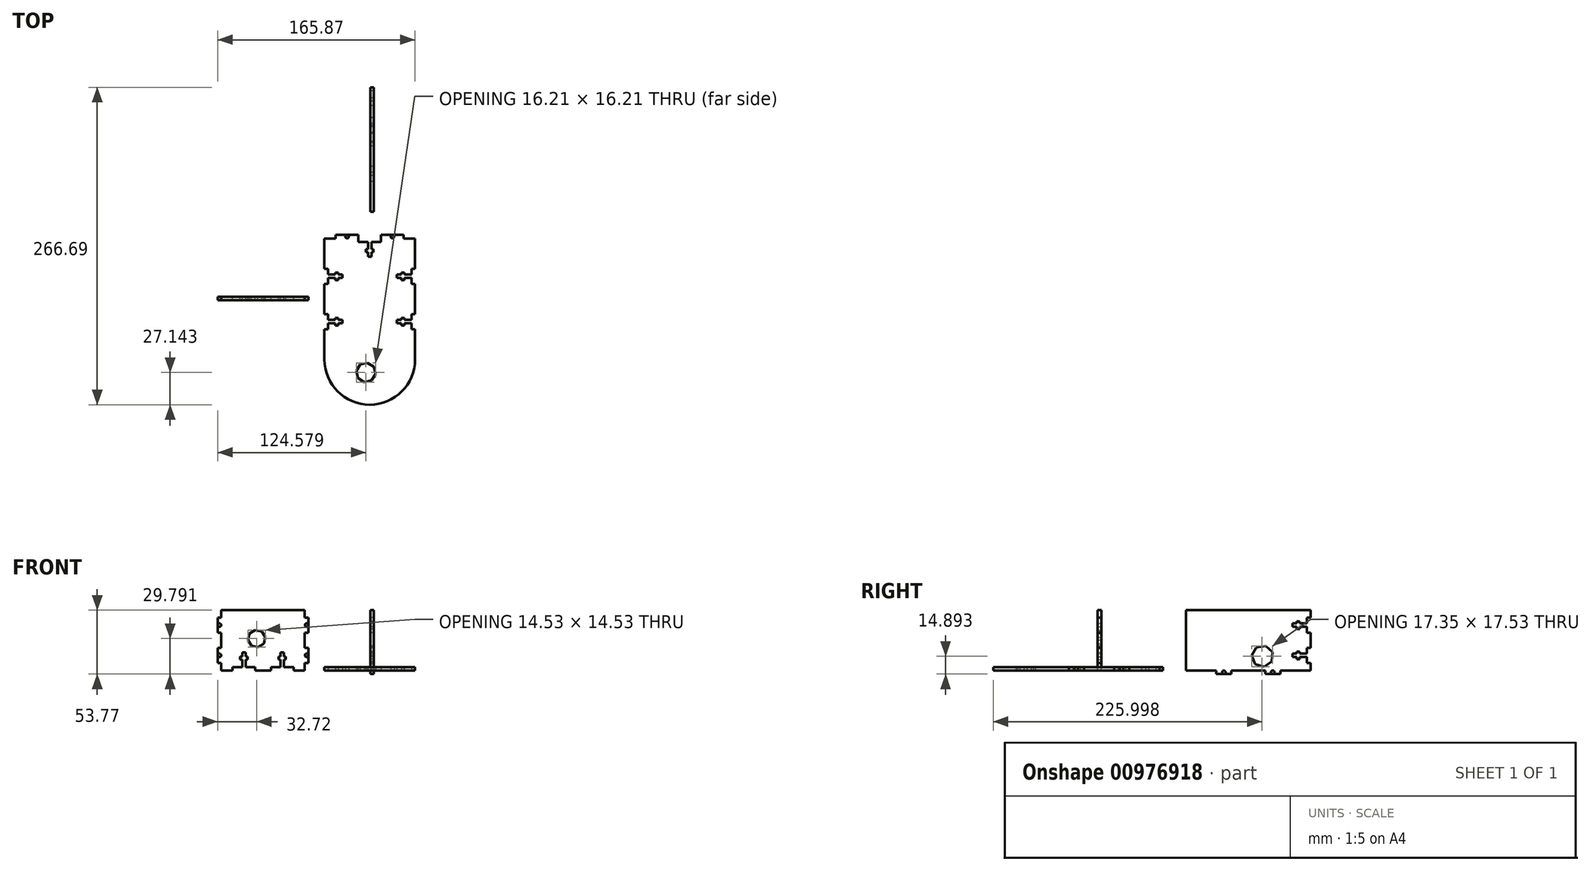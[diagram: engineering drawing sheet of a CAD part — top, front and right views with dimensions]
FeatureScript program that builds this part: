
annotation { "Feature Type Name" : "Feature", "Feature Type Description" : "" }
export const myFeature = defineFeature(function(context is Context, id is Id, definition is map)
    precondition{}
    {
        {
            var Q0;
            Q0=qCreatedBy(makeId("Top.planeOp"),FACE);
            var sketch = newSketch(context, id + "F0", { "sketchPlane" : qUnion([Q0])});
            skLineSegment(sketch, "E0.bottom", {"start": v(-38.64, 48.88) * mm, "end": v(-29.12, 48.88) * mm});
            skLineSegment(sketch, "E0.left", {"start": v(-38.64, 48.88) * mm, "end": v(-38.64, 23.48) * mm});
            skLineSegment(sketch, "E0.right", {"start": v(37.56, 48.88) * mm, "end": v(37.56, 23.48) * mm});
            skCircle(sketch, "E1", {"center": v(-19.6, 50.33) * mm, "radius": 1.42 * mm});
            skCircle(sketch, "E2", {"center": v(18.5, 50.33) * mm, "radius": 1.42 * mm});
            skLineSegment(sketch, "E3.bottom", {"start": v(-29.12, 51.85) * mm, "end": v(-10.07, 51.85) * mm});
            skLineSegment(sketch, "E3.left", {"start": v(-29.12, 51.85) * mm, "end": v(-29.12, 48.88) * mm});
            skLineSegment(sketch, "E3.right", {"start": v(-10.07, 51.85) * mm, "end": v(-10.07, 48.88) * mm});
            skLineSegment(sketch, "E4.top", {"start": v(28.03, 51.85) * mm, "end": v(8.98, 51.85) * mm});
            skLineSegment(sketch, "E4.left", {"start": v(28.03, 48.88) * mm, "end": v(28.03, 51.85) * mm});
            skLineSegment(sketch, "E4.right", {"start": v(8.98, 48.88) * mm, "end": v(8.98, 51.85) * mm});
            skLineSegment(sketch, "E5", {"start": v(-10.07, 48.88) * mm, "end": v(-10.07, 45.9) * mm});
            skLineSegment(sketch, "E6", {"start": v(-10.07, 45.9) * mm, "end": v(-1.96, 45.9) * mm});
            skLineSegment(sketch, "E7", {"start": v(8.98, 45.9) * mm, "end": v(8.98, 48.88) * mm});
            skLineSegment(sketch, "E8", {"start": v(-1.96, 45.9) * mm, "end": v(-1.96, 39.76) * mm});
            skLineSegment(sketch, "E9", {"start": v(-1.96, 39.76) * mm, "end": v(-3.7, 39.76) * mm});
            skLineSegment(sketch, "E10", {"start": v(-3.7, 39.76) * mm, "end": v(-3.7, 37.22) * mm});
            skLineSegment(sketch, "E11", {"start": v(-3.7, 37.22) * mm, "end": v(-1.96, 37.22) * mm});
            skLineSegment(sketch, "E12", {"start": v(-1.96, 37.22) * mm, "end": v(-1.96, 33.64) * mm});
            skLineSegment(sketch, "E13", {"start": v(-1.96, 33.64) * mm, "end": v(0.88, 33.64) * mm});
            skLineSegment(sketch, "E14", {"start": v(0.88, 33.64) * mm, "end": v(0.88, 37.22) * mm});
            skLineSegment(sketch, "E15", {"start": v(0.88, 37.22) * mm, "end": v(2.6, 37.22) * mm});
            skLineSegment(sketch, "E16", {"start": v(2.6, 37.22) * mm, "end": v(2.6, 39.76) * mm});
            skLineSegment(sketch, "E17", {"start": v(2.6, 39.76) * mm, "end": v(0.88, 39.76) * mm});
            skLineSegment(sketch, "E18", {"start": v(0.88, 39.76) * mm, "end": v(0.88, 45.9) * mm});
            skLineSegment(sketch, "E19.trimOffspring", {"start": v(28.03, 48.88) * mm, "end": v(37.56, 48.88) * mm});
            skLineSegment(sketch, "E20.bottom", {"start": v(37.56, 23.48) * mm, "end": v(34.59, 23.48) * mm});
            skLineSegment(sketch, "E20.top", {"start": v(37.56, 10.78) * mm, "end": v(34.59, 10.78) * mm});
            skLineSegment(sketch, "E20.right", {"start": v(34.59, 23.48) * mm, "end": v(34.59, 18.55) * mm});
            skLineSegment(sketch, "E21", {"start": v(34.59, 18.55) * mm, "end": v(28.44, 18.55) * mm});
            skLineSegment(sketch, "E22", {"start": v(28.44, 18.55) * mm, "end": v(28.44, 20.28) * mm});
            skLineSegment(sketch, "E23", {"start": v(28.44, 20.28) * mm, "end": v(25.9, 20.28) * mm});
            skLineSegment(sketch, "E24", {"start": v(25.9, 20.28) * mm, "end": v(25.9, 18.55) * mm});
            skLineSegment(sketch, "E25", {"start": v(25.9, 18.55) * mm, "end": v(22.32, 18.55) * mm});
            skLineSegment(sketch, "E26", {"start": v(22.32, 18.55) * mm, "end": v(22.32, 15.7) * mm});
            skLineSegment(sketch, "E27", {"start": v(22.32, 15.7) * mm, "end": v(25.9, 15.7) * mm});
            skLineSegment(sketch, "E28", {"start": v(25.9, 15.7) * mm, "end": v(25.9, 13.98) * mm});
            skLineSegment(sketch, "E29", {"start": v(25.9, 13.98) * mm, "end": v(28.44, 13.98) * mm});
            skLineSegment(sketch, "E30", {"start": v(28.44, 13.98) * mm, "end": v(28.44, 15.7) * mm});
            skLineSegment(sketch, "E31", {"start": v(28.44, 15.7) * mm, "end": v(34.59, 15.7) * mm});
            skLineSegment(sketch, "E32.trimOffspring", {"start": v(0.88, 45.9) * mm, "end": v(8.98, 45.9) * mm});
            skLineSegment(sketch, "E33", {"start": v(37.56, -14.62) * mm, "end": v(34.59, -14.62) * mm});
            skLineSegment(sketch, "E34", {"start": v(34.59, -14.62) * mm, "end": v(34.59, -19.55) * mm});
            skLineSegment(sketch, "E35", {"start": v(34.59, -27.32) * mm, "end": v(37.56, -27.32) * mm});
            skLineSegment(sketch, "E36.trimOffspring", {"start": v(34.59, 15.7) * mm, "end": v(34.59, 10.78) * mm});
            skLineSegment(sketch, "E37.trimOffspring", {"start": v(37.56, 10.78) * mm, "end": v(37.56, -14.62) * mm});
            skLineSegment(sketch, "E38", {"start": v(34.59, -19.55) * mm, "end": v(28.44, -19.55) * mm});
            skLineSegment(sketch, "E39", {"start": v(28.44, -19.55) * mm, "end": v(28.44, -17.82) * mm});
            skLineSegment(sketch, "E40", {"start": v(28.44, -17.82) * mm, "end": v(25.9, -17.82) * mm});
            skLineSegment(sketch, "E41", {"start": v(25.9, -17.82) * mm, "end": v(25.9, -19.55) * mm});
            skLineSegment(sketch, "E42", {"start": v(25.9, -19.55) * mm, "end": v(22.32, -19.55) * mm});
            skLineSegment(sketch, "E43", {"start": v(22.32, -19.55) * mm, "end": v(22.32, -22.4) * mm});
            skLineSegment(sketch, "E44", {"start": v(22.32, -22.4) * mm, "end": v(25.9, -22.4) * mm});
            skLineSegment(sketch, "E45", {"start": v(25.9, -22.4) * mm, "end": v(25.9, -24.12) * mm});
            skLineSegment(sketch, "E46", {"start": v(25.9, -24.12) * mm, "end": v(28.44, -24.12) * mm});
            skLineSegment(sketch, "E47", {"start": v(28.44, -24.12) * mm, "end": v(28.44, -22.4) * mm});
            skLineSegment(sketch, "E48", {"start": v(28.44, -22.4) * mm, "end": v(34.59, -22.4) * mm});
            skLineSegment(sketch, "E49.trimOffspring", {"start": v(37.56, -27.32) * mm, "end": v(37.56, -52.72) * mm});
            skLineSegment(sketch, "E50.trimOffspring", {"start": v(34.59, -22.4) * mm, "end": v(34.59, -27.32) * mm});
            skLineSegment(sketch, "E51", {"start": v(-38.64, -27.32) * mm, "end": v(-35.67, -27.32) * mm});
            skLineSegment(sketch, "E52", {"start": v(-35.67, -27.32) * mm, "end": v(-35.67, -22.4) * mm});
            skLineSegment(sketch, "E53", {"start": v(-35.67, -14.62) * mm, "end": v(-38.64, -14.62) * mm});
            skLineSegment(sketch, "E54", {"start": v(-35.67, -22.4) * mm, "end": v(-29.52, -22.4) * mm});
            skLineSegment(sketch, "E55", {"start": v(-29.52, -22.4) * mm, "end": v(-29.52, -24.12) * mm});
            skLineSegment(sketch, "E56", {"start": v(-29.52, -24.12) * mm, "end": v(-26.98, -24.12) * mm});
            skLineSegment(sketch, "E57", {"start": v(-26.98, -24.12) * mm, "end": v(-26.98, -22.4) * mm});
            skLineSegment(sketch, "E58", {"start": v(-26.98, -22.4) * mm, "end": v(-23.4, -22.4) * mm});
            skLineSegment(sketch, "E59", {"start": v(-23.4, -22.4) * mm, "end": v(-23.4, -19.55) * mm});
            skLineSegment(sketch, "E60", {"start": v(-23.4, -19.55) * mm, "end": v(-26.98, -19.55) * mm});
            skLineSegment(sketch, "E61", {"start": v(-26.98, -19.55) * mm, "end": v(-26.98, -17.82) * mm});
            skLineSegment(sketch, "E62", {"start": v(-26.98, -17.82) * mm, "end": v(-29.52, -17.82) * mm});
            skLineSegment(sketch, "E63", {"start": v(-29.52, -17.82) * mm, "end": v(-29.52, -19.55) * mm});
            skLineSegment(sketch, "E64", {"start": v(-29.52, -19.55) * mm, "end": v(-35.67, -19.55) * mm});
            skLineSegment(sketch, "E65.trimOffspring", {"start": v(-35.67, -19.55) * mm, "end": v(-35.67, -14.62) * mm});
            skLineSegment(sketch, "E66.trimOffspring", {"start": v(-38.64, -27.32) * mm, "end": v(-38.64, -52.72) * mm});
            skLineSegment(sketch, "E67", {"start": v(-38.64, 23.48) * mm, "end": v(-35.67, 23.48) * mm});
            skLineSegment(sketch, "E68", {"start": v(-35.67, 23.48) * mm, "end": v(-35.67, 18.55) * mm});
            skLineSegment(sketch, "E69", {"start": v(-35.67, 10.78) * mm, "end": v(-38.64, 10.78) * mm});
            skLineSegment(sketch, "E70", {"start": v(-35.67, 18.55) * mm, "end": v(-29.52, 18.55) * mm});
            skLineSegment(sketch, "E71", {"start": v(-29.52, 18.55) * mm, "end": v(-29.52, 20.28) * mm});
            skLineSegment(sketch, "E72", {"start": v(-29.52, 20.28) * mm, "end": v(-26.98, 20.28) * mm});
            skLineSegment(sketch, "E73", {"start": v(-26.98, 20.28) * mm, "end": v(-26.98, 18.55) * mm});
            skLineSegment(sketch, "E74", {"start": v(-26.98, 18.55) * mm, "end": v(-23.4, 18.55) * mm});
            skLineSegment(sketch, "E75", {"start": v(-23.4, 18.55) * mm, "end": v(-23.4, 15.7) * mm});
            skLineSegment(sketch, "E76", {"start": v(-23.4, 15.7) * mm, "end": v(-26.98, 15.7) * mm});
            skLineSegment(sketch, "E77", {"start": v(-26.98, 15.7) * mm, "end": v(-26.98, 13.98) * mm});
            skLineSegment(sketch, "E78", {"start": v(-26.98, 13.98) * mm, "end": v(-29.52, 13.98) * mm});
            skLineSegment(sketch, "E79", {"start": v(-29.52, 13.98) * mm, "end": v(-29.52, 15.7) * mm});
            skLineSegment(sketch, "E80", {"start": v(-29.52, 15.7) * mm, "end": v(-35.67, 15.7) * mm});
            skLineSegment(sketch, "E81.trimOffspring", {"start": v(-35.67, 15.7) * mm, "end": v(-35.67, 10.78) * mm});
            skLineSegment(sketch, "E82.trimOffspring", {"start": v(-38.64, 10.78) * mm, "end": v(-38.64, -14.62) * mm});
            skArc(sketch, "E83", {"start": v(-38.64, -52.72) * mm, "mid": v(-0.54, -90.82) * mm, "end": v(37.56, -52.72) * mm});
            skLineSegment(sketch, "E84.0", {"start": v(4.37, -65.01) * mm, "end": v(1.06, -70.35) * mm});
            skLineSegment(sketch, "E84.1", {"start": v(1.06, -70.35) * mm, "end": v(-5.07, -71.78) * mm});
            skLineSegment(sketch, "E84.2", {"start": v(-5.07, -71.78) * mm, "end": v(-10.4, -68.46) * mm});
            skLineSegment(sketch, "E84.3", {"start": v(-10.4, -68.46) * mm, "end": v(-11.84, -62.34) * mm});
            skLineSegment(sketch, "E84.4", {"start": v(-11.84, -62.34) * mm, "end": v(-8.52, -57) * mm});
            skLineSegment(sketch, "E84.5", {"start": v(-8.52, -57) * mm, "end": v(-2.4, -55.57) * mm});
            skLineSegment(sketch, "E84.6", {"start": v(-2.4, -55.57) * mm, "end": v(2.94, -58.9) * mm});
            skLineSegment(sketch, "E84.7", {"start": v(2.94, -58.9) * mm, "end": v(4.37, -65.01) * mm});
            skPoint(sketch, "E84.0.midPoint", {"position": v(2.71, -67.68) * mm});
            skSolve(sketch);
        }
        {
            var Q0;
            Q0=qCreatedBy(makeId("Right.planeOp"),FACE);
            var sketch = newSketch(context, id + "F1", { "sketchPlane" : qUnion([Q0])});
            skLineSegment(sketch, "E85", {"start": v(71.3, 0) * mm, "end": v(96.7, 0) * mm});
            skLineSegment(sketch, "E86", {"start": v(175.87, 0) * mm, "end": v(175.87, 6.35) * mm});
            skLineSegment(sketch, "E87", {"start": v(175.87, 50.8) * mm, "end": v(71.3, 50.8) * mm});
            skLineSegment(sketch, "E88", {"start": v(71.3, 50.8) * mm, "end": v(71.3, 44.45) * mm});
            skLineSegment(sketch, "E89", {"start": v(175.87, 44.45) * mm, "end": v(172.9, 44.45) * mm});
            skLineSegment(sketch, "E90", {"start": v(172.9, 44.45) * mm, "end": v(172.9, 39.52) * mm});
            skLineSegment(sketch, "E91", {"start": v(172.9, 31.75) * mm, "end": v(175.87, 31.75) * mm});
            skLineSegment(sketch, "E92", {"start": v(175.87, 19.05) * mm, "end": v(172.9, 19.05) * mm});
            skLineSegment(sketch, "E93", {"start": v(172.9, 19.05) * mm, "end": v(172.9, 14.12) * mm});
            skLineSegment(sketch, "E94", {"start": v(172.9, 6.35) * mm, "end": v(175.87, 6.35) * mm});
            skLineSegment(sketch, "E95", {"start": v(172.9, 39.52) * mm, "end": v(166.75, 39.52) * mm});
            skLineSegment(sketch, "E96", {"start": v(166.75, 39.52) * mm, "end": v(166.75, 41.25) * mm});
            skLineSegment(sketch, "E97", {"start": v(166.75, 41.25) * mm, "end": v(164.2, 41.25) * mm});
            skLineSegment(sketch, "E98", {"start": v(164.2, 41.25) * mm, "end": v(164.2, 39.52) * mm});
            skLineSegment(sketch, "E99", {"start": v(164.2, 39.52) * mm, "end": v(160.63, 39.52) * mm});
            skLineSegment(sketch, "E100", {"start": v(160.63, 39.52) * mm, "end": v(160.63, 36.68) * mm});
            skLineSegment(sketch, "E101", {"start": v(160.63, 36.68) * mm, "end": v(164.2, 36.68) * mm});
            skLineSegment(sketch, "E102", {"start": v(164.2, 36.68) * mm, "end": v(164.2, 34.95) * mm});
            skLineSegment(sketch, "E103", {"start": v(164.2, 34.95) * mm, "end": v(166.75, 34.95) * mm});
            skLineSegment(sketch, "E104", {"start": v(166.75, 34.95) * mm, "end": v(166.75, 36.68) * mm});
            skLineSegment(sketch, "E105", {"start": v(166.75, 36.68) * mm, "end": v(172.9, 36.68) * mm});
            skLineSegment(sketch, "E106.trimOffspring", {"start": v(172.9, 36.68) * mm, "end": v(172.9, 31.75) * mm});
            skLineSegment(sketch, "E107.trimOffspring", {"start": v(175.87, 44.45) * mm, "end": v(175.87, 50.8) * mm});
            skLineSegment(sketch, "E108", {"start": v(172.9, 14.12) * mm, "end": v(166.75, 14.12) * mm});
            skLineSegment(sketch, "E109", {"start": v(166.75, 14.12) * mm, "end": v(166.75, 15.85) * mm});
            skLineSegment(sketch, "E110", {"start": v(166.75, 15.85) * mm, "end": v(164.2, 15.85) * mm});
            skLineSegment(sketch, "E111", {"start": v(164.2, 15.85) * mm, "end": v(164.2, 14.12) * mm});
            skLineSegment(sketch, "E112", {"start": v(164.2, 14.12) * mm, "end": v(160.63, 14.12) * mm});
            skLineSegment(sketch, "E113", {"start": v(160.63, 14.12) * mm, "end": v(160.63, 11.28) * mm});
            skLineSegment(sketch, "E114", {"start": v(160.63, 11.28) * mm, "end": v(164.2, 11.28) * mm});
            skLineSegment(sketch, "E115", {"start": v(164.2, 11.28) * mm, "end": v(164.2, 9.55) * mm});
            skLineSegment(sketch, "E116", {"start": v(164.2, 9.55) * mm, "end": v(166.75, 9.55) * mm});
            skLineSegment(sketch, "E117", {"start": v(166.75, 9.55) * mm, "end": v(166.75, 11.28) * mm});
            skLineSegment(sketch, "E118", {"start": v(166.75, 11.28) * mm, "end": v(172.9, 11.28) * mm});
            skLineSegment(sketch, "E119.trimOffspring", {"start": v(172.9, 11.28) * mm, "end": v(172.9, 6.35) * mm});
            skLineSegment(sketch, "E120.trimOffspring", {"start": v(175.87, 19.05) * mm, "end": v(175.87, 31.75) * mm});
            skLineSegment(sketch, "E121.top", {"start": v(137.77, -2.97) * mm, "end": v(150.47, -2.97) * mm});
            skLineSegment(sketch, "E121.left", {"start": v(137.77, 0) * mm, "end": v(137.77, -2.97) * mm});
            skLineSegment(sketch, "E121.right", {"start": v(150.47, 0) * mm, "end": v(150.47, -2.97) * mm});
            skLineSegment(sketch, "E122.trimOffspring", {"start": v(150.47, 0) * mm, "end": v(175.87, 0) * mm});
            skLineSegment(sketch, "E123.top", {"start": v(96.7, -2.97) * mm, "end": v(109.4, -2.97) * mm});
            skLineSegment(sketch, "E123.left", {"start": v(96.7, 0) * mm, "end": v(96.7, -2.97) * mm});
            skLineSegment(sketch, "E123.right", {"start": v(109.4, 0) * mm, "end": v(109.4, -2.97) * mm});
            skLineSegment(sketch, "E124.trimOffspring", {"start": v(109.4, 0) * mm, "end": v(137.77, 0) * mm});
            skCircle(sketch, "E125", {"center": v(103.04, -1.45) * mm, "radius": 1.42 * mm});
            skCircle(sketch, "E126", {"center": v(144.12, -1.45) * mm, "radius": 1.42 * mm});
            skLineSegment(sketch, "E127.trimOffspring", {"start": v(71.3, 31.75) * mm, "end": v(71.3, 19.05) * mm});
            skLineSegment(sketch, "E128.trimOffspring", {"start": v(71.3, 6.35) * mm, "end": v(71.3, 0) * mm});
            skLineSegment(sketch, "E129", {"start": v(71.3, 44.45) * mm, "end": v(71.3, 31.75) * mm});
            skLineSegment(sketch, "E130", {"start": v(71.3, 19.05) * mm, "end": v(71.3, 6.35) * mm});
            skLineSegment(sketch, "E131.0", {"start": v(126.5, 12.67) * mm, "end": v(130.36, 19.47) * mm});
            skLineSegment(sketch, "E131.1", {"start": v(130.36, 19.47) * mm, "end": v(138.09, 20.69) * mm});
            skLineSegment(sketch, "E131.2", {"start": v(138.09, 20.69) * mm, "end": v(143.85, 15.4) * mm});
            skLineSegment(sketch, "E131.3", {"start": v(143.85, 15.4) * mm, "end": v(143.32, 7.6) * mm});
            skLineSegment(sketch, "E131.4", {"start": v(143.32, 7.6) * mm, "end": v(136.9, 3.16) * mm});
            skLineSegment(sketch, "E131.5", {"start": v(136.9, 3.16) * mm, "end": v(129.4, 5.41) * mm});
            skLineSegment(sketch, "E131.6", {"start": v(129.4, 5.41) * mm, "end": v(126.5, 12.67) * mm});
            skPoint(sketch, "E131.0.midPoint", {"position": v(128.43, 16.07) * mm});
            skSolve(sketch);
        }
        {
            var Q0;
            Q0=qCreatedBy(makeId("Front.planeOp"),FACE);
            var sketch = newSketch(context, id + "F2", { "sketchPlane" : qUnion([Q0])});
            skLineSegment(sketch, "E132", {"start": v(-125.34, 0) * mm, "end": v(-115.82, 0) * mm});
            skLineSegment(sketch, "E133", {"start": v(-55.09, 0) * mm, "end": v(-55.09, 6.35) * mm});
            skLineSegment(sketch, "E134", {"start": v(-55.09, 50.8) * mm, "end": v(-125.34, 50.8) * mm});
            skLineSegment(sketch, "E135", {"start": v(-125.34, 50.8) * mm, "end": v(-125.34, 44.45) * mm});
            skLineSegment(sketch, "E136", {"start": v(-64.61, 0) * mm, "end": v(-64.61, 2.97) * mm});
            skLineSegment(sketch, "E137", {"start": v(-64.61, 2.97) * mm, "end": v(-72.71, 2.97) * mm});
            skLineSegment(sketch, "E138", {"start": v(-83.66, 2.97) * mm, "end": v(-83.66, 0) * mm});
            skLineSegment(sketch, "E139", {"start": v(-72.71, 2.97) * mm, "end": v(-72.71, 9.12) * mm});
            skLineSegment(sketch, "E140", {"start": v(-72.71, 9.12) * mm, "end": v(-70.99, 9.12) * mm});
            skLineSegment(sketch, "E141", {"start": v(-70.99, 9.12) * mm, "end": v(-70.99, 11.66) * mm});
            skLineSegment(sketch, "E142", {"start": v(-70.99, 11.66) * mm, "end": v(-72.75, 11.66) * mm});
            skLineSegment(sketch, "E143", {"start": v(-72.75, 11.66) * mm, "end": v(-72.75, 15.13) * mm});
            skLineSegment(sketch, "E144", {"start": v(-72.75, 15.13) * mm, "end": v(-75.52, 15.13) * mm});
            skLineSegment(sketch, "E145", {"start": v(-75.52, 15.13) * mm, "end": v(-75.52, 11.66) * mm});
            skLineSegment(sketch, "E146", {"start": v(-75.52, 11.66) * mm, "end": v(-77.29, 11.66) * mm});
            skLineSegment(sketch, "E147", {"start": v(-77.29, 11.66) * mm, "end": v(-77.29, 9.12) * mm});
            skLineSegment(sketch, "E148", {"start": v(-77.29, 9.12) * mm, "end": v(-75.56, 9.12) * mm});
            skLineSegment(sketch, "E149", {"start": v(-75.56, 9.12) * mm, "end": v(-75.56, 2.97) * mm});
            skLineSegment(sketch, "E150.trimOffspring", {"start": v(-75.56, 2.97) * mm, "end": v(-83.66, 2.97) * mm});
            skLineSegment(sketch, "E151", {"start": v(-96.77, 0) * mm, "end": v(-96.77, 2.97) * mm});
            skLineSegment(sketch, "E152", {"start": v(-96.77, 2.97) * mm, "end": v(-104.87, 2.97) * mm});
            skLineSegment(sketch, "E153", {"start": v(-115.82, 2.97) * mm, "end": v(-115.82, 0) * mm});
            skLineSegment(sketch, "E154", {"start": v(-104.87, 2.97) * mm, "end": v(-104.87, 9.12) * mm});
            skLineSegment(sketch, "E155", {"start": v(-104.87, 9.12) * mm, "end": v(-103.14, 9.12) * mm});
            skLineSegment(sketch, "E156", {"start": v(-103.14, 9.12) * mm, "end": v(-103.14, 11.66) * mm});
            skLineSegment(sketch, "E157", {"start": v(-103.14, 11.66) * mm, "end": v(-104.87, 11.66) * mm});
            skLineSegment(sketch, "E158", {"start": v(-104.87, 11.66) * mm, "end": v(-104.87, 15.14) * mm});
            skLineSegment(sketch, "E159", {"start": v(-104.87, 15.14) * mm, "end": v(-107.71, 15.14) * mm});
            skLineSegment(sketch, "E160", {"start": v(-107.71, 15.14) * mm, "end": v(-107.71, 11.66) * mm});
            skLineSegment(sketch, "E161", {"start": v(-107.71, 11.66) * mm, "end": v(-109.44, 11.66) * mm});
            skLineSegment(sketch, "E162", {"start": v(-109.44, 11.66) * mm, "end": v(-109.44, 9.12) * mm});
            skLineSegment(sketch, "E163", {"start": v(-109.44, 9.12) * mm, "end": v(-107.71, 9.12) * mm});
            skLineSegment(sketch, "E164", {"start": v(-107.71, 9.12) * mm, "end": v(-107.71, 2.97) * mm});
            skLineSegment(sketch, "E165.trimOffspring", {"start": v(-107.71, 2.97) * mm, "end": v(-115.82, 2.97) * mm});
            skLineSegment(sketch, "E166.bottom", {"start": v(-55.09, 44.45) * mm, "end": v(-52.11, 44.45) * mm});
            skLineSegment(sketch, "E166.top", {"start": v(-55.09, 31.75) * mm, "end": v(-52.11, 31.75) * mm});
            skLineSegment(sketch, "E166.right", {"start": v(-52.11, 44.45) * mm, "end": v(-52.11, 31.75) * mm});
            skLineSegment(sketch, "E167.bottom", {"start": v(-55.09, 19.05) * mm, "end": v(-52.11, 19.05) * mm});
            skLineSegment(sketch, "E167.top", {"start": v(-55.09, 6.35) * mm, "end": v(-52.11, 6.35) * mm});
            skLineSegment(sketch, "E167.right", {"start": v(-52.11, 19.05) * mm, "end": v(-52.11, 6.35) * mm});
            skLineSegment(sketch, "E168.trimOffspring", {"start": v(-55.09, 44.45) * mm, "end": v(-55.09, 50.8) * mm});
            skLineSegment(sketch, "E169.trimOffspring", {"start": v(-55.09, 19.05) * mm, "end": v(-55.09, 31.75) * mm});
            skCircle(sketch, "E170", {"center": v(-53.64, 38.1) * mm, "radius": 1.42 * mm});
            skCircle(sketch, "E171", {"center": v(-53.64, 12.7) * mm, "radius": 1.42 * mm});
            skLineSegment(sketch, "E172.bottom", {"start": v(-125.34, 44.45) * mm, "end": v(-128.31, 44.45) * mm});
            skLineSegment(sketch, "E172.top", {"start": v(-125.34, 31.75) * mm, "end": v(-128.31, 31.75) * mm});
            skLineSegment(sketch, "E172.right", {"start": v(-128.31, 44.45) * mm, "end": v(-128.31, 31.75) * mm});
            skLineSegment(sketch, "E173.bottom", {"start": v(-125.34, 19.05) * mm, "end": v(-128.31, 19.05) * mm});
            skLineSegment(sketch, "E173.top", {"start": v(-125.34, 6.35) * mm, "end": v(-128.31, 6.35) * mm});
            skLineSegment(sketch, "E173.right", {"start": v(-128.31, 19.05) * mm, "end": v(-128.31, 6.35) * mm});
            skLineSegment(sketch, "E174.trimOffspring", {"start": v(-125.34, 31.75) * mm, "end": v(-125.34, 19.05) * mm});
            skLineSegment(sketch, "E175.trimOffspring", {"start": v(-125.34, 6.35) * mm, "end": v(-125.34, 0) * mm});
            skCircle(sketch, "E176", {"center": v(-126.8, 38.1) * mm, "radius": 1.42 * mm});
            skCircle(sketch, "E177", {"center": v(-126.8, 12.7) * mm, "radius": 1.42 * mm});
            skLineSegment(sketch, "E178.trimOffspring", {"start": v(-96.77, 0) * mm, "end": v(-83.66, 0) * mm});
            skLineSegment(sketch, "E179.trimOffspring", {"start": v(-64.61, 0) * mm, "end": v(-55.09, 0) * mm});
            skLineSegment(sketch, "E180.0", {"start": v(-99.93, 20.88) * mm, "end": v(-102.85, 25.69) * mm});
            skLineSegment(sketch, "E180.1", {"start": v(-102.85, 25.69) * mm, "end": v(-101.53, 31.16) * mm});
            skLineSegment(sketch, "E180.2", {"start": v(-101.53, 31.16) * mm, "end": v(-96.72, 34.09) * mm});
            skLineSegment(sketch, "E180.3", {"start": v(-96.72, 34.09) * mm, "end": v(-91.25, 32.76) * mm});
            skLineSegment(sketch, "E180.4", {"start": v(-91.25, 32.76) * mm, "end": v(-88.33, 27.95) * mm});
            skLineSegment(sketch, "E180.5", {"start": v(-88.33, 27.95) * mm, "end": v(-89.65, 22.49) * mm});
            skLineSegment(sketch, "E180.6", {"start": v(-89.65, 22.49) * mm, "end": v(-94.46, 19.56) * mm});
            skLineSegment(sketch, "E180.7", {"start": v(-94.46, 19.56) * mm, "end": v(-99.93, 20.88) * mm});
            skPoint(sketch, "E180.0.midPoint", {"position": v(-101.4, 23.29) * mm});
            skSolve(sketch);
        }
        {
            var Q0;
            Q0=makeQuery(id+"F1.imprint","IMPRINT",FACE,{"disambiguationData":[TD([[makeQuery(id+"F1.imprint","IMPRINT",EDGE,{"derivedFrom":sQuery(id+"F1.wireOp",EDGE,"E85")}),1.0]])]});
            extrude(context, id + "F3", {"entities" : qUnion([Q0]), "depth" : 2.97 * mm, "offsetDistance" : 25.4 * mm});
        }
        {
            var Q0;
            Q0=makeQuery(id+"F2.imprint","IMPRINT",FACE,{"disambiguationData":[TD([[makeQuery(id+"F2.imprint","IMPRINT",EDGE,{"derivedFrom":sQuery(id+"F2.wireOp",EDGE,"E132")}),1.0]])]});
            extrude(context, id + "F4", {"entities" : qUnion([Q0]), "depth" : 2.97 * mm, "offsetDistance" : 25.4 * mm});
        }
        {
            var Q0;
            Q0=makeQuery(id+"F0.imprint","IMPRINT",FACE,{"disambiguationData":[TD([[makeQuery(id+"F0.imprint","IMPRINT",EDGE,{"derivedFrom":sQuery(id+"F0.wireOp",EDGE,"E0.bottom")}),-1.0]])]});
            extrude(context, id + "F5", {"entities" : qUnion([Q0]), "depth" : 2.97 * mm, "offsetDistance" : 25.4 * mm});
        }
    });
